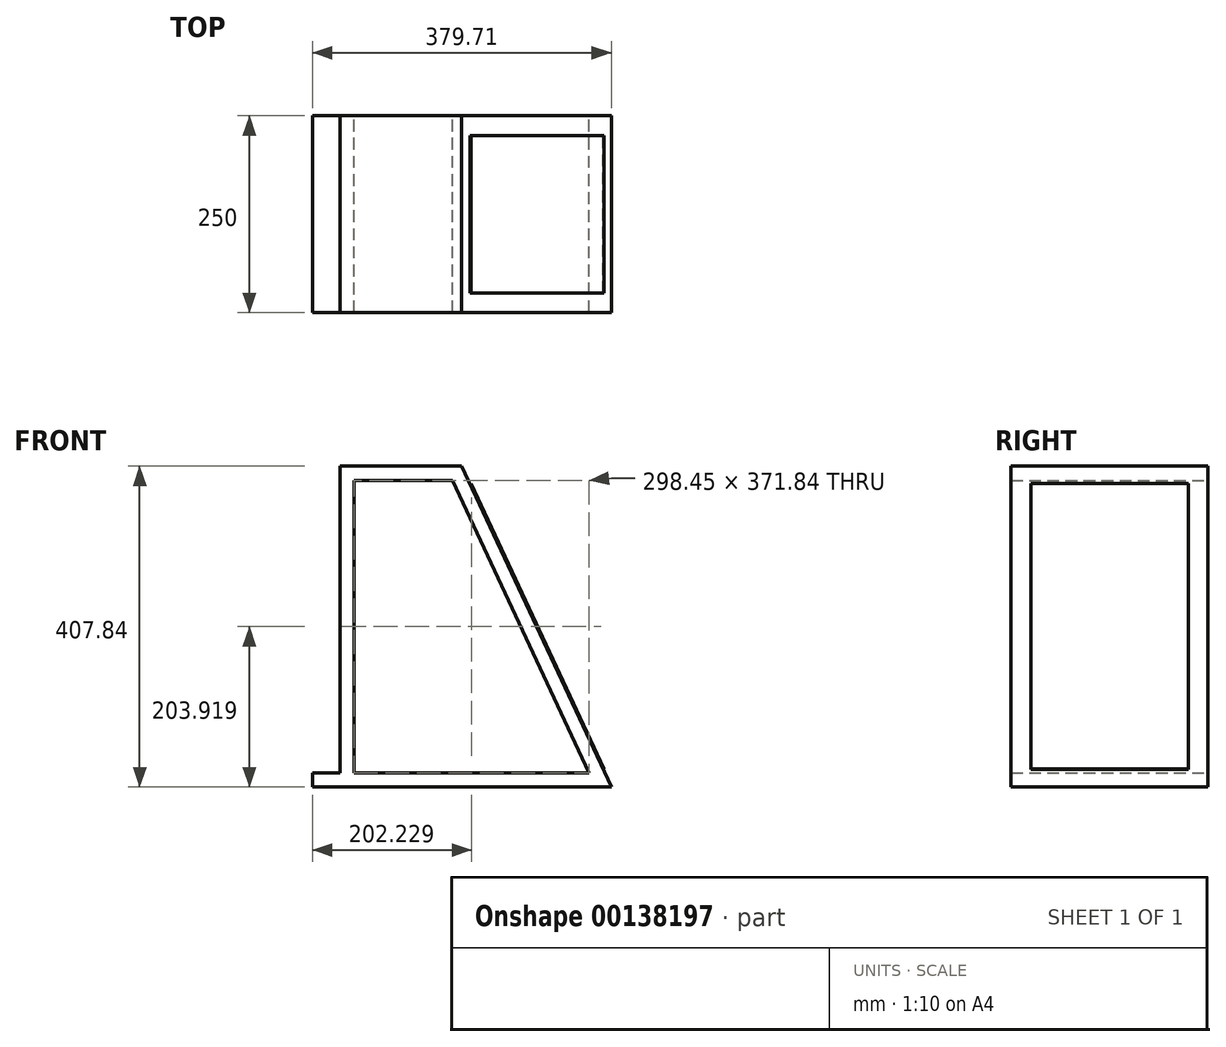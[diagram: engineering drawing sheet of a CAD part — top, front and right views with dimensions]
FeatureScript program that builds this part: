
annotation { "Feature Type Name" : "Feature", "Feature Type Description" : "" }
export const myFeature = defineFeature(function(context is Context, id is Id, definition is map)
    precondition{}
    {
        {
            var Q0;
            Q0=qCreatedBy(makeId("Front.planeOp"),FACE);
            var sketch = newSketch(context, id + "F0", { "sketchPlane" : qUnion([Q0])});
            skLineSegment(sketch, "E0", {"start": v(-153.18, 0) * mm, "end": v(226.53, 0) * mm});
            skLineSegment(sketch, "E1", {"start": v(226.53, 0) * mm, "end": v(36.35, 407.84) * mm});
            skLineSegment(sketch, "E2", {"start": v(36.35, 407.84) * mm, "end": v(-118.18, 407.84) * mm});
            skLineSegment(sketch, "E3", {"start": v(-118.18, 407.84) * mm, "end": v(-118.18, 18) * mm});
            skLineSegment(sketch, "E4", {"start": v(-118.18, 18) * mm, "end": v(-153.18, 18) * mm});
            skLineSegment(sketch, "E5", {"start": v(-153.18, 18) * mm, "end": v(-153.18, 0) * mm});
            skPoint(sketch, "E6.orphan", {"position": v(-155.33, 0) * mm});
            skSolve(sketch);
        }
        {
            var Q0;
            Q0=makeQuery(id+"F0.imprint","IMPRINT",FACE,{"disambiguationData":[TD([[makeQuery(id+"F0.imprint","IMPRINT",EDGE,{"derivedFrom":sQuery(id+"F0.wireOp",EDGE,"E0")}),1.0]])]});
            extrude(context, id + "F1", {"entities" : qUnion([Q0]), "depth" : 250 * mm});
        }
        {
            var Q0;
            Q0=makeQuery(id+"F1.opExtrude","CAP_FACE",FACE,{"disambiguationData":[OSD([sQuery(id+"F0.wireOp",EDGE,"E0"),sQuery(id+"F0.wireOp",EDGE,"E1"),sQuery(id+"F0.wireOp",EDGE,"E2"),sQuery(id+"F0.wireOp",EDGE,"E3"),sQuery(id+"F0.wireOp",EDGE,"E4"),sQuery(id+"F0.wireOp",EDGE,"E5")])],"isStart":true});
            var sketch = newSketch(context, id + "F2", { "sketchPlane" : qUnion([Q0])});
            skLineSegment(sketch, "E7.0", {"start": v(-198.28, 18) * mm, "end": v(135.18, 18) * mm});
            skLineSegment(sketch, "E7.1", {"start": v(135.18, 0) * mm, "end": v(100.18, 0) * mm});
            skLineSegment(sketch, "E7.2", {"start": v(100.18, 0) * mm, "end": v(100.18, 389.84) * mm});
            skLineSegment(sketch, "E7.3", {"start": v(135.18, 0) * mm, "end": v(135.18, 18) * mm});
            skLineSegment(sketch, "E7.4", {"start": v(100.18, 389.84) * mm, "end": v(-24.88, 389.84) * mm});
            skLineSegment(sketch, "E7.5", {"start": v(-24.88, 389.84) * mm, "end": v(-198.28, 18) * mm});
            skLineSegment(sketch, "E8.0", {"start": v(-218.68, 5) * mm, "end": v(148.18, 5) * mm});
            skLineSegment(sketch, "E8.1", {"start": v(148.18, 13) * mm, "end": v(113.18, 13) * mm});
            skLineSegment(sketch, "E8.2", {"start": v(113.18, 13) * mm, "end": v(113.18, 402.84) * mm});
            skLineSegment(sketch, "E8.3", {"start": v(148.18, 5) * mm, "end": v(148.18, 13) * mm});
            skLineSegment(sketch, "E8.4", {"start": v(113.18, 402.84) * mm, "end": v(-33.17, 402.84) * mm});
            skLineSegment(sketch, "E8.5", {"start": v(-33.17, 402.84) * mm, "end": v(-218.68, 5) * mm});
            skSolve(sketch);
        }
        {
            var Q0;
            {var subQ4=sQuery(id+"F2.wireOp",EDGE,"E7.4");Q0=makeQuery(id+"F2.imprint","IMPRINT",FACE,{"disambiguationData":[TD([[makeQuery(id+"F2.imprint","IMPRINT",EDGE,{"derivedFrom":subQ4}),1.0]])]});}
            extrude(context, id + "F3", {"entities" : qUnion([Q0]), "operationType" : NewBodyOperationType.REMOVE, "endBound" : BoundingType.THROUGH_ALL, "oppositeDirection" : true, "depth" : 25 * mm});
        }
        {
            var Q0;
            Q0=makeQuery(id+"F1.opExtrude","SWEPT_FACE",FACE,{"disambiguationData":[OSD([sQuery(id+"F0.wireOp",EDGE,"E1")])]});
            var sketch = newSketch(context, id + "F4", { "sketchPlane" : qUnion([Q0])});
            skLineSegment(sketch, "E9.bottom", {"start": v(-225, 329.26) * mm, "end": v(-25, 329.26) * mm});
            skLineSegment(sketch, "E9.top", {"start": v(-225, -70.74) * mm, "end": v(-25, -70.74) * mm});
            skLineSegment(sketch, "E9.left", {"start": v(-225, 329.26) * mm, "end": v(-225, -70.74) * mm});
            skLineSegment(sketch, "E9.right", {"start": v(-25, 329.26) * mm, "end": v(-25, -70.74) * mm});
            skLineSegment(sketch, "E10.bottom", {"start": v(-225, 329.26) * mm, "end": v(-250, 329.26) * mm, "construction": true});
            skLineSegment(sketch, "E10.top", {"start": v(-225, 329.26) * mm, "end": v(-250, 329.26) * mm, "construction": true});
            skLineSegment(sketch, "E10.left", {"start": v(-225, 329.26) * mm, "end": v(-225, 329.26) * mm});
            skLineSegment(sketch, "E10.right", {"start": v(-250, 329.26) * mm, "end": v(-250, 329.26) * mm});
            skLineSegment(sketch, "E11.bottom", {"start": v(-25, 329.26) * mm, "end": v(0, 329.26) * mm, "construction": true});
            skLineSegment(sketch, "E11.top", {"start": v(-25, 329.26) * mm, "end": v(0, 329.26) * mm, "construction": true});
            skLineSegment(sketch, "E11.left", {"start": v(-25, 329.26) * mm, "end": v(-25, 329.26) * mm});
            skLineSegment(sketch, "E11.right", {"start": v(0, 329.26) * mm, "end": v(0, 329.26) * mm});
            skLineSegment(sketch, "E12.top", {"start": v(-25, 354.26) * mm, "end": v(-25, 354.26) * mm});
            skLineSegment(sketch, "E12.left", {"start": v(-25, 329.26) * mm, "end": v(-25, 354.26) * mm, "construction": true});
            skLineSegment(sketch, "E12.right", {"start": v(-25, 329.26) * mm, "end": v(-25, 354.26) * mm, "construction": true});
            skLineSegment(sketch, "E13.top", {"start": v(-225, 354.26) * mm, "end": v(-225, 354.26) * mm});
            skLineSegment(sketch, "E13.left", {"start": v(-225, 329.26) * mm, "end": v(-225, 354.26) * mm, "construction": true});
            skLineSegment(sketch, "E13.right", {"start": v(-225, 329.26) * mm, "end": v(-225, 354.26) * mm, "construction": true});
            skLineSegment(sketch, "E14.bottom", {"start": v(-225, -70.74) * mm, "end": v(-250, -70.74) * mm, "construction": true});
            skLineSegment(sketch, "E14.top", {"start": v(-225, -70.74) * mm, "end": v(-250, -70.74) * mm, "construction": true});
            skLineSegment(sketch, "E14.left", {"start": v(-225, -70.74) * mm, "end": v(-225, -70.74) * mm});
            skLineSegment(sketch, "E14.right", {"start": v(-250, -70.74) * mm, "end": v(-250, -70.74) * mm});
            skLineSegment(sketch, "E15.bottom", {"start": v(-226.22, -70.74) * mm, "end": v(-225, -70.74) * mm, "construction": true});
            skLineSegment(sketch, "E15.top", {"start": v(-226.22, -95.74) * mm, "end": v(-225, -95.74) * mm, "construction": true});
            skLineSegment(sketch, "E15.left", {"start": v(-225, -70.74) * mm, "end": v(-225, -95.74) * mm, "construction": true});
            skLineSegment(sketch, "E15.right", {"start": v(-226.22, -70.74) * mm, "end": v(-226.22, -95.74) * mm, "construction": true});
            skLineSegment(sketch, "E16.bottom", {"start": v(-25, -70.74) * mm, "end": v(-25, -70.74) * mm});
            skLineSegment(sketch, "E16.top", {"start": v(-25, -95.74) * mm, "end": v(-25, -95.74) * mm});
            skLineSegment(sketch, "E16.left", {"start": v(-25, -70.74) * mm, "end": v(-25, -95.74) * mm, "construction": true});
            skLineSegment(sketch, "E16.right", {"start": v(-25, -70.74) * mm, "end": v(-25, -95.74) * mm, "construction": true});
            skLineSegment(sketch, "E17.bottom", {"start": v(-25, -70.74) * mm, "end": v(0, -70.74) * mm, "construction": true});
            skLineSegment(sketch, "E17.top", {"start": v(-25, -70.74) * mm, "end": v(0, -70.74) * mm, "construction": true});
            skLineSegment(sketch, "E17.right", {"start": v(0, -70.74) * mm, "end": v(0, -70.74) * mm});
            skSolve(sketch);
        }
        {
            var Q0;
            Q0=makeQuery(id+"F4.imprint","IMPRINT",FACE,{"disambiguationData":[TD([[makeQuery(id+"F4.imprint","IMPRINT",EDGE,{"derivedFrom":sQuery(id+"F4.wireOp",EDGE,"E9.bottom")}),-1.0]])]});
            extrude(context, id + "F5", {"entities" : qUnion([Q0]), "operationType" : NewBodyOperationType.ADD, "depth" : 1.5 * mm});
        }
    });
